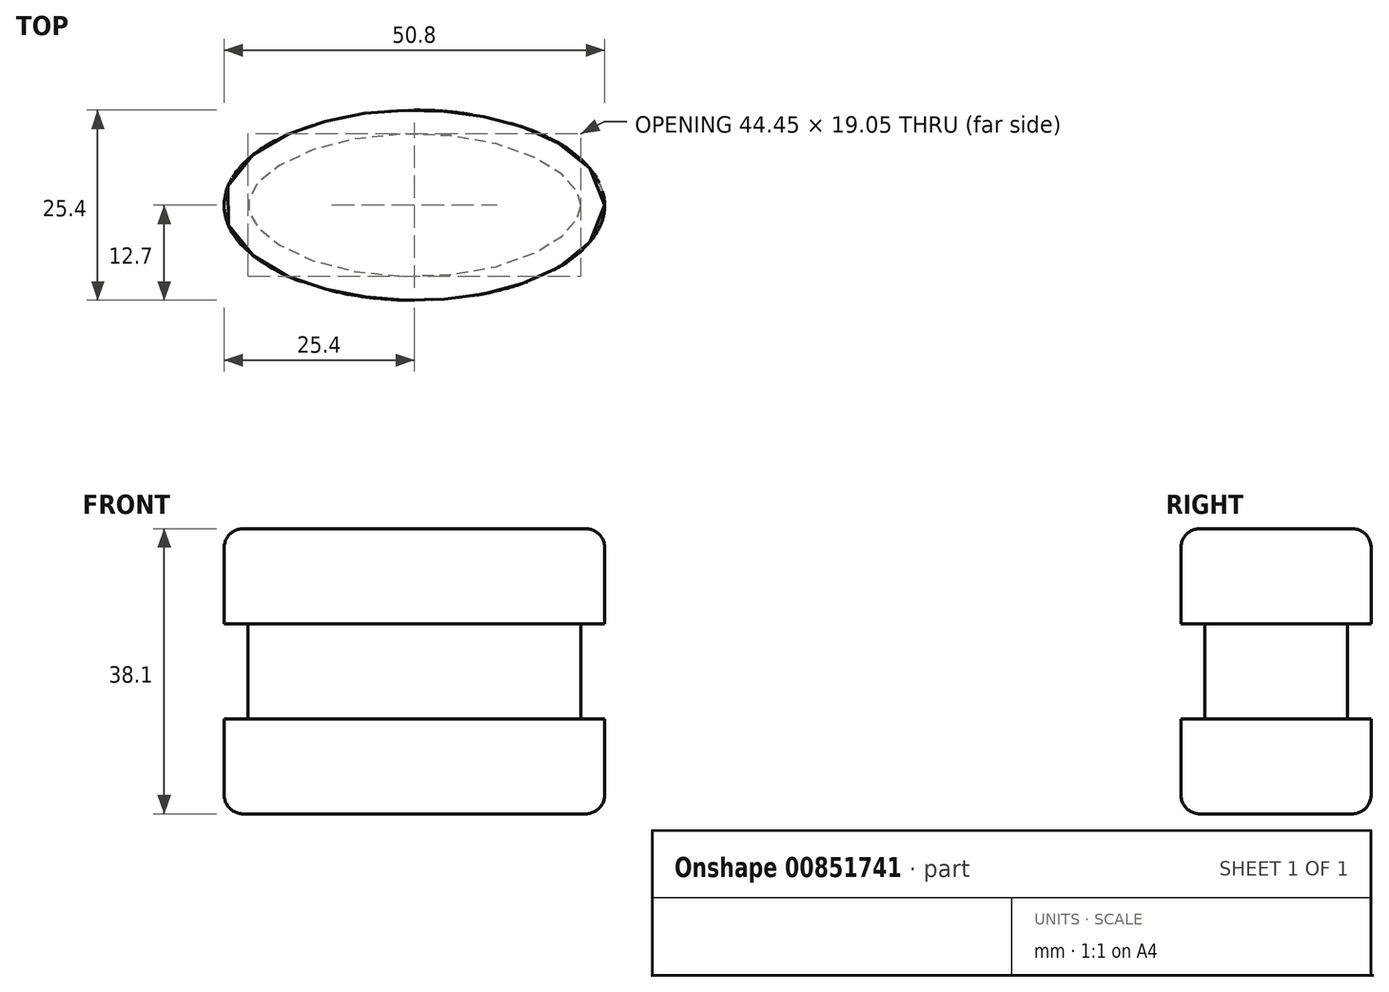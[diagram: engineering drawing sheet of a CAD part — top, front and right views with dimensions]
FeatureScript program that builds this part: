
annotation { "Feature Type Name" : "Feature", "Feature Type Description" : "" }
export const myFeature = defineFeature(function(context is Context, id is Id, definition is map)
    precondition{}
    {
        {
            var Q0;
            Q0=qCreatedBy(makeId("Top.planeOp"),FACE);
            var sketch = newSketch(context, id + "F0", { "sketchPlane" : qUnion([Q0])});
            skLineSegment(sketch, "E0.bottom", {"start": v(25.4, -12.7) * mm, "end": v(-25.4, -12.7) * mm, "construction": true});
            skLineSegment(sketch, "E0.top", {"start": v(25.4, 12.7) * mm, "end": v(-25.4, 12.7) * mm, "construction": true});
            skLineSegment(sketch, "E0.left", {"start": v(25.4, -12.7) * mm, "end": v(25.4, 12.7) * mm, "construction": true});
            skLineSegment(sketch, "E0.right", {"start": v(-25.4, -12.7) * mm, "end": v(-25.4, 12.7) * mm, "construction": true});
            skPoint(sketch, "E0.middle", {"position": v(0, 0) * mm});
            skEllipse(sketch, "E1", {"center": v(0, 0) * mm, "majorRadius": 25.4 * mm, "minorRadius": 12.7 * mm, "majorAxis": v(1, 0)});
            skSolve(sketch);
        }
        {
            var Q0;
            Q0=makeQuery(id+"F0.imprint","IMPRINT",FACE,{"disambiguationData":[TD([[makeQuery(id+"F0.imprint","IMPRINT",EDGE,{"derivedFrom":sQuery(id+"F0.wireOp",EDGE,"E1")}),1.0]])]});
            extrude(context, id + "F1", {"entities" : qUnion([Q0]), "depth" : 38.1 * mm, "offsetDistance" : 25.4 * mm});
        }
        {
            var Q0;
            Q0=qCreatedBy(makeId("Front.planeOp"),FACE);
            var sketch = newSketch(context, id + "F2", { "sketchPlane" : qUnion([Q0])});
            skLineSegment(sketch, "E2.bottom", {"start": v(25.4, 25.4) * mm, "end": v(22.23, 25.4) * mm});
            skLineSegment(sketch, "E2.top", {"start": v(25.4, 12.7) * mm, "end": v(22.23, 12.7) * mm});
            skLineSegment(sketch, "E2.left", {"start": v(25.4, 25.4) * mm, "end": v(25.4, 12.7) * mm});
            skLineSegment(sketch, "E2.right", {"start": v(22.23, 25.4) * mm, "end": v(22.23, 12.7) * mm});
            skSolve(sketch);
        }
        {
            var Q0;
            Q0=makeQuery(id+"F2.imprint","IMPRINT",FACE,{"disambiguationData":[TD([[makeQuery(id+"F2.imprint","IMPRINT",EDGE,{"derivedFrom":sQuery(id+"F2.wireOp",EDGE,"E2.bottom")}),1.0]])]});
            var Q1;
            Q1=makeQuery(id+"F1.opExtrude","CAP_EDGE",EDGE,{"disambiguationData":[OSD([sQuery(id+"F0.wireOp",EDGE,"E1")])],"isStart":false});
            sweep(context, id + "F3", {"operationType" : NewBodyOperationType.REMOVE, "profiles" : qUnion([Q0]), "path" : qUnion([Q1])});
        }
        {
            var Q0;
            Q0=makeQuery(id+"F1.opExtrude","CAP_EDGE",EDGE,{"disambiguationData":[OSD([sQuery(id+"F0.wireOp",EDGE,"E1")])],"isStart":false});
            var Q1;
            Q1=makeQuery(id+"F1.opExtrude","CAP_EDGE",EDGE,{"disambiguationData":[OSD([sQuery(id+"F0.wireOp",EDGE,"E1")])],"isStart":true});
            fillet(context, id + "F4", {"entities" : qUnion([Q0, Q1]), "radius" : 2.54 * mm, "tangentPropagation" : true, "allowEdgeOverflow" : false});
        }
    });
